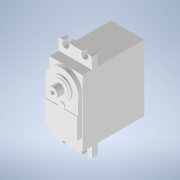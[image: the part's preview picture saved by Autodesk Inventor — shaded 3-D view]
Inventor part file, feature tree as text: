
AUTODESK INVENTOR PART (.ipt)
format: ipt  version: 2022 (Build 260153000, 153)  size: 235,008 bytes
history: native  units: mm
features: extrude x7, sketch x7, projected_geometry x4, fillet x1
ambient origin geometry x8: Origin, YZ Plane, XZ Plane, XY Plane, X Axis, Y Axis, Z Axis, Center Point
bodies: Solid1 (feature_tree)
feature tree (19):
  extrude  "Extrusion1"  Depth=54.0mm
  extrude  "Extrusion2"  Depth=28.0mm
  extrude  "Extrusion3"  Depth=3.6mm
  extrude  "Extrusion4"  Depth=20.0mm TaperAngle=0.0deg
  extrude  "Extrusion5"  Depth=2.6mm
  extrude  "Extrusion6"  Depth=20.6mm
  extrude  "Extrusion7"  Depth=3.6mm
  fillet  "Fillet1"  Radius=2.0mm
  sketch  "Sketch1"  dims[d0=38.0mm d1=54.0mm]
  sketch  "Sketch2"  dims[d3=40.0mm d4=28.0mm]
  projected_geometry  "Projected Loop1"
  sketch  "Sketch3"  dims[d5=47.2mm d6=3.6mm]
  sketch  "Sketch4"  dims[d7=5.65mm d8=20.0mm d9=0.0mm]
  projected_geometry  "Projected Loop4"
  sketch  "Sketch5"  dims[d11=9.7mm d12=2.6mm]
  sketch  "Sketch6"  dims[d13=6.0mm d14=20.6mm]
  sketch  "Sketch7"  dims[d15=2.5mm d16=0.0mm d19=9.0mm d20=2.0mm d21=12.7mm d25=2.1mm d26=3.75mm d27=0.5mm d28=0.0mm d29=13.0mm d30=1.0mm d31=0.0mm d32=10.5mm d33=0.4mm d34=0.0mm d35=6.0mm d36=2.6mm d37=4.3mm d38=0.0mm d39=3.0mm d40=2.5mm d42=2.15mm d44=2.5mm d45=2.15mm d46=4.3mm d47=0.0mm d48=1.0mm d49=28.0mm d50=5.65mm d51=3.6mm]
  projected_geometry  "Projected Loop5"
  projected_geometry  "Projected Loop6"
